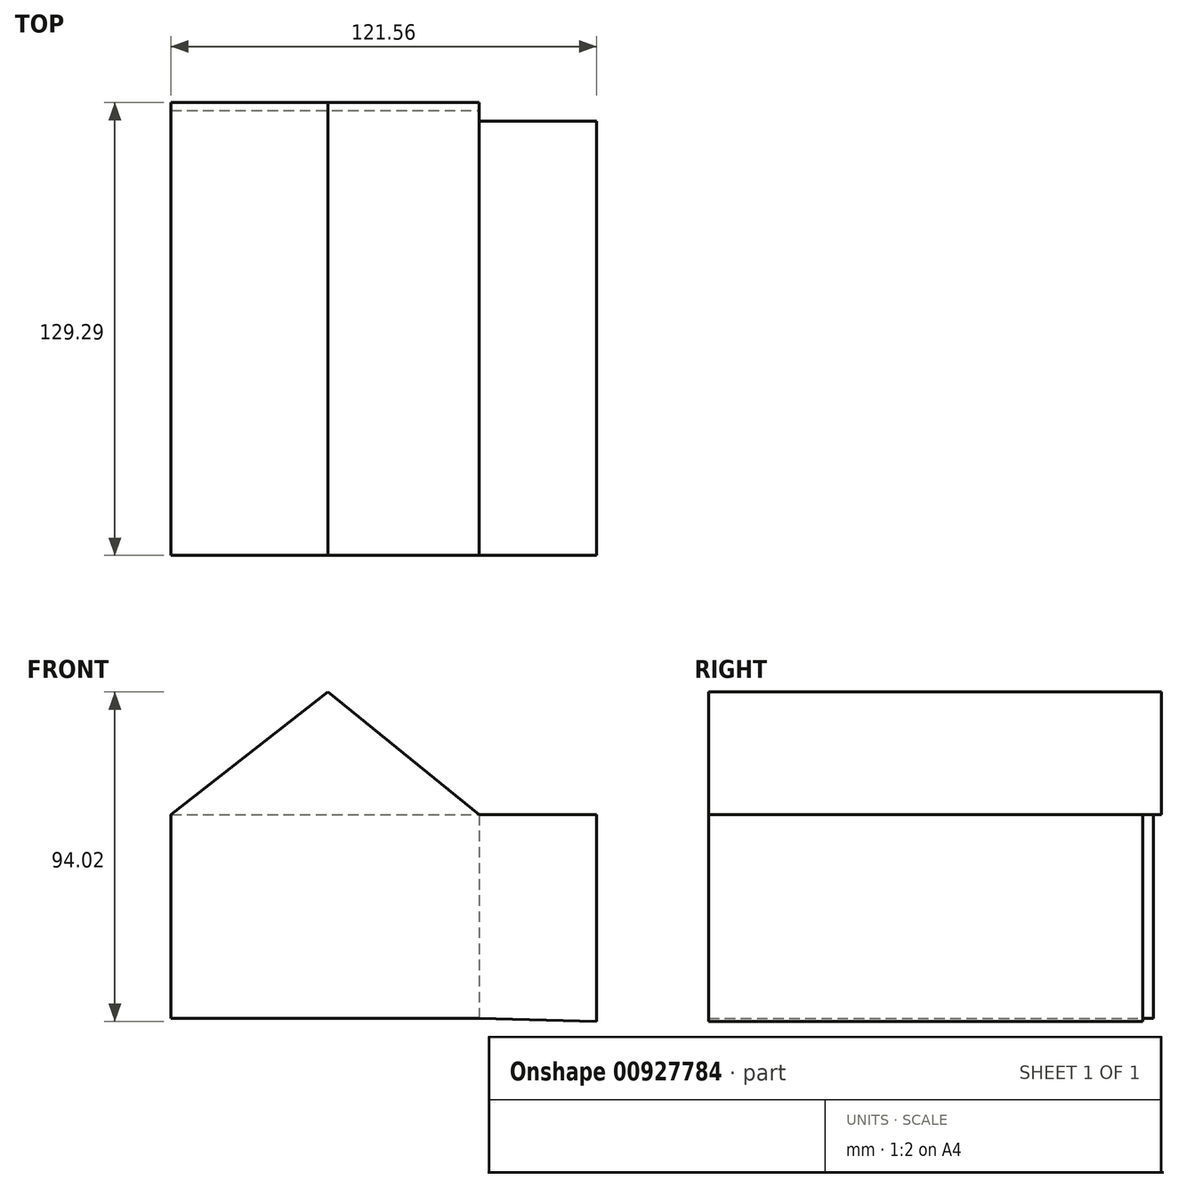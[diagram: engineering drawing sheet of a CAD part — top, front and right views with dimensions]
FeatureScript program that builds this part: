
annotation { "Feature Type Name" : "Feature", "Feature Type Description" : "" }
export const myFeature = defineFeature(function(context is Context, id is Id, definition is map)
    precondition{}
    {
        {
            var Q0;
            Q0=qCreatedBy(makeId("Front.planeOp"),FACE);
            var sketch = newSketch(context, id + "F0", { "sketchPlane" : qUnion([Q0])});
            skLineSegment(sketch, "E0.bottom", {"start": v(-44.9, 31.4) * mm, "end": v(43.05, 31.4) * mm});
            skLineSegment(sketch, "E0.top", {"start": v(-44.9, -26.72) * mm, "end": v(43.05, -26.72) * mm});
            skLineSegment(sketch, "E0.left", {"start": v(-44.9, 31.4) * mm, "end": v(-44.9, -26.72) * mm});
            skLineSegment(sketch, "E0.right", {"start": v(43.05, 31.4) * mm, "end": v(43.05, -26.72) * mm});
            skSolve(sketch);
        }
        {
            var Q0;
            Q0 = qSketchRegion(id + "F0", true);
            var Q1;
            Q1=makeQuery(id+"F0.imprint","IMPRINT",FACE,{"disambiguationData":[TD([[makeQuery(id+"F0.imprint","IMPRINT",EDGE,{"derivedFrom":sQuery(id+"F0.wireOp",EDGE,"E0.bottom")}),-1.0]])]});
            extrude(context, id + "F1", {"entities" : qUnion([Q0, Q1]), "depth" : 127 * mm, "offsetDistance" : 25.4 * mm});
        }
        {
            var Q0;
            Q0=makeQuery(id+"F1.opExtrude","CAP_FACE",FACE,{"disambiguationData":[OSD([sQuery(id+"F0.wireOp",EDGE,"E0.bottom"),sQuery(id+"F0.wireOp",EDGE,"E0.top"),sQuery(id+"F0.wireOp",EDGE,"E0.left"),sQuery(id+"F0.wireOp",EDGE,"E0.right")])],"isStart":false});
            var sketch = newSketch(context, id + "F2", { "sketchPlane" : qUnion([Q0])});
            skLineSegment(sketch, "E1", {"start": v(0, 5.6) * mm, "end": v(29.25, 5.6) * mm});
            skLineSegment(sketch, "E2", {"start": v(-44.9, 31.4) * mm, "end": v(0, 66.43) * mm});
            skLineSegment(sketch, "E3", {"start": v(43.05, 31.4) * mm, "end": v(0, 66.43) * mm});
            skSolve(sketch);
        }
        {
            var Q0;
            Q0=makeQuery(id+"F2.imprint","IMPRINT",FACE,{"disambiguationData":[TD([[makeQuery(id+"F2.imprint","IMPRINT",EDGE,{"derivedFrom":sQuery(id+"F2.wireOp",EDGE,"E2")}),-1.0]])]});
            extrude(context, id + "F3", {"entities" : qUnion([Q0]), "operationType" : NewBodyOperationType.ADD, "oppositeDirection" : true, "depth" : 129.29 * mm, "offsetDistance" : 25.4 * mm});
        }
        {
            var Q0;
            {var subQ0=sQuery(id+"F0.wireOp",EDGE,"E0.bottom");Q0=makeQuery(id+"F3.boolean.opBoolean","MERGE",FACE,{"derivedFrom":[makeQuery(id+"F1.opExtrude","CAP_FACE",FACE,{"disambiguationData":[OSD([subQ0,sQuery(id+"F0.wireOp",EDGE,"E0.top"),sQuery(id+"F0.wireOp",EDGE,"E0.left"),sQuery(id+"F0.wireOp",EDGE,"E0.right")])],"isStart":false}),makeQuery(id+"F3.opExtrude","CAP_FACE",FACE,{"disambiguationData":[OSD([subQ0,sQuery(id+"F2.wireOp",EDGE,"E2"),sQuery(id+"F2.wireOp",EDGE,"E3")])],"isStart":true})]});}
            var sketch = newSketch(context, id + "F4", { "sketchPlane" : qUnion([Q0])});
            skLineSegment(sketch, "E4", {"start": v(43.05, 31.4) * mm, "end": v(76.65, 31.4) * mm});
            skLineSegment(sketch, "E5", {"start": v(76.65, 31.4) * mm, "end": v(76.65, -27.6) * mm});
            skLineSegment(sketch, "E6", {"start": v(76.65, -27.6) * mm, "end": v(43.05, -26.72) * mm});
            skSolve(sketch);
        }
        {
            var Q0;
            Q0=makeQuery(id+"F4.imprint","IMPRINT",FACE,{"disambiguationData":[TD([[makeQuery(id+"F4.imprint","IMPRINT",EDGE,{"derivedFrom":sQuery(id+"F4.wireOp",EDGE,"E4")}),-1.0]])]});
            extrude(context, id + "F5", {"entities" : qUnion([Q0]), "operationType" : NewBodyOperationType.ADD, "oppositeDirection" : true, "depth" : 123.95 * mm, "offsetDistance" : 25.4 * mm});
        }
    });
